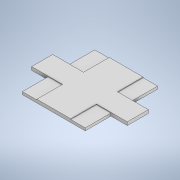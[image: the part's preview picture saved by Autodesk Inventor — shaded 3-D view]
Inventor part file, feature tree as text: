
AUTODESK INVENTOR PART (.ipt)
format: ipt  version: 2022 (Build 260153000, 153)  size: 142,336 bytes
history: native  units: mm
features: extrude x3, sketch x3, projected_geometry x1
ambient origin geometry x8: Origin, YZ Plane, XZ Plane, XY Plane, X Axis, Y Axis, Z Axis, Center Point
bodies: Solid1 (feature_tree)
feature tree (7):
  extrude  "Extrusion1"  Depth=191.0mm
  extrude  "Extrusion2"  Depth=191.0mm
  extrude  "Extrusion4"  Depth=78.0mm
  sketch  "Sketch1"  dims[d0=220.0mm d1=191.0mm]
  sketch  "Sketch2"  dims[d2=10.0mm d3=0.0mm d4=191.0mm]
  projected_geometry  "Projected Loop1"
  sketch  "Sketch4"  dims[d5=220.0mm d6=78.0mm d7=78.0mm d8=78.0mm d9=78.0mm d10=44.0mm d11=44.0mm d12=44.0mm d13=44.0mm d14=2.0mm d15=0.0mm d18=50.0mm d19=50.0mm d20=10.0mm d21=0.0mm]
